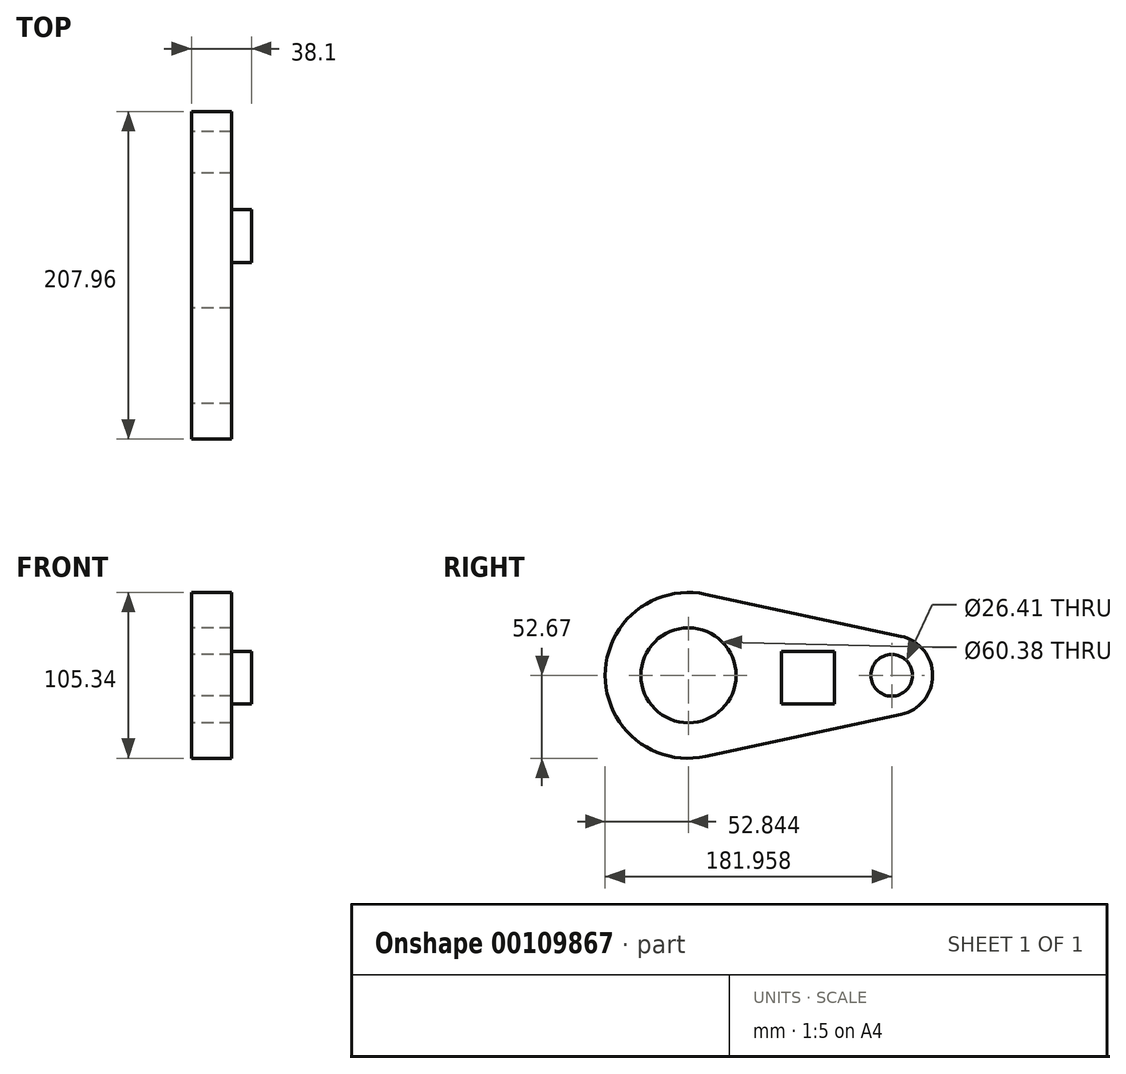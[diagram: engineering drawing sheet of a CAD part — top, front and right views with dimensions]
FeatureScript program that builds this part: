
annotation { "Feature Type Name" : "Feature", "Feature Type Description" : "" }
export const myFeature = defineFeature(function(context is Context, id is Id, definition is map)
    precondition{}
    {
        {
            var Q0;
            Q0=qCreatedBy(makeId("Right.planeOp"),FACE);
            var sketch = newSketch(context, id + "F0", { "sketchPlane" : qUnion([Q0])});
            skCircle(sketch, "E0", {"center": v(-75.25, 0) * mm, "radius": 52.67 * mm});
            skCircle(sketch, "E1", {"center": v(54.64, 0) * mm, "radius": 25.4 * mm});
            skLineSegment(sketch, "E2", {"start": v(59.98, 24.83) * mm, "end": v(-64.2, 51.5) * mm});
            skLineSegment(sketch, "E3", {"start": v(59.98, -24.83) * mm, "end": v(-64.2, -51.5) * mm});
            skSolve(sketch);
        }
        {
            var Q0;
            Q0 = qSketchRegion(id + "F0", true);
            extrude(context, id + "F1", {"entities" : qUnion([Q0]), "depth" : 25.4 * mm});
        }
        {
            var Q0;
            Q0=qCreatedBy(makeId("Right.planeOp"),FACE);
            var sketch = newSketch(context, id + "F2", { "sketchPlane" : qUnion([Q0])});
            skCircle(sketch, "E4", {"center": v(-75.08, 0) * mm, "radius": 30.2 * mm});
            skCircle(sketch, "E5", {"center": v(54.04, 0) * mm, "radius": 13.2 * mm});
            skSolve(sketch);
        }
        {
            var Q0;
            Q0 = qSketchRegion(id + "F2", true);
            var Q1;
            Q1=sQuery(id+"F2.wireOp",EDGE,"E4");
            extrude(context, id + "F3", {"entities" : qUnion([Q0]), "operationType" : NewBodyOperationType.REMOVE, "surfaceEntities" : qUnion([Q1]), "depth" : 46.73 * mm});
        }
        {
            var Q0;
            Q0=qCreatedBy(makeId("Right.planeOp"),FACE);
            var sketch = newSketch(context, id + "F4", { "sketchPlane" : qUnion([Q0])});
            skLineSegment(sketch, "E6.bottom", {"start": v(17.67, 15.36) * mm, "end": v(-15.92, 15.36) * mm});
            skLineSegment(sketch, "E6.top", {"start": v(17.67, -18.23) * mm, "end": v(-15.92, -18.23) * mm});
            skLineSegment(sketch, "E6.left", {"start": v(17.67, 15.36) * mm, "end": v(17.67, -18.23) * mm});
            skLineSegment(sketch, "E6.right", {"start": v(-15.92, 15.36) * mm, "end": v(-15.92, -18.23) * mm});
            skSolve(sketch);
        }
        {
            var Q0;
            Q0 = qSketchRegion(id + "F4", true);
            extrude(context, id + "F5", {"entities" : qUnion([Q0]), "operationType" : NewBodyOperationType.ADD, "depth" : 38.1 * mm});
        }
    });
